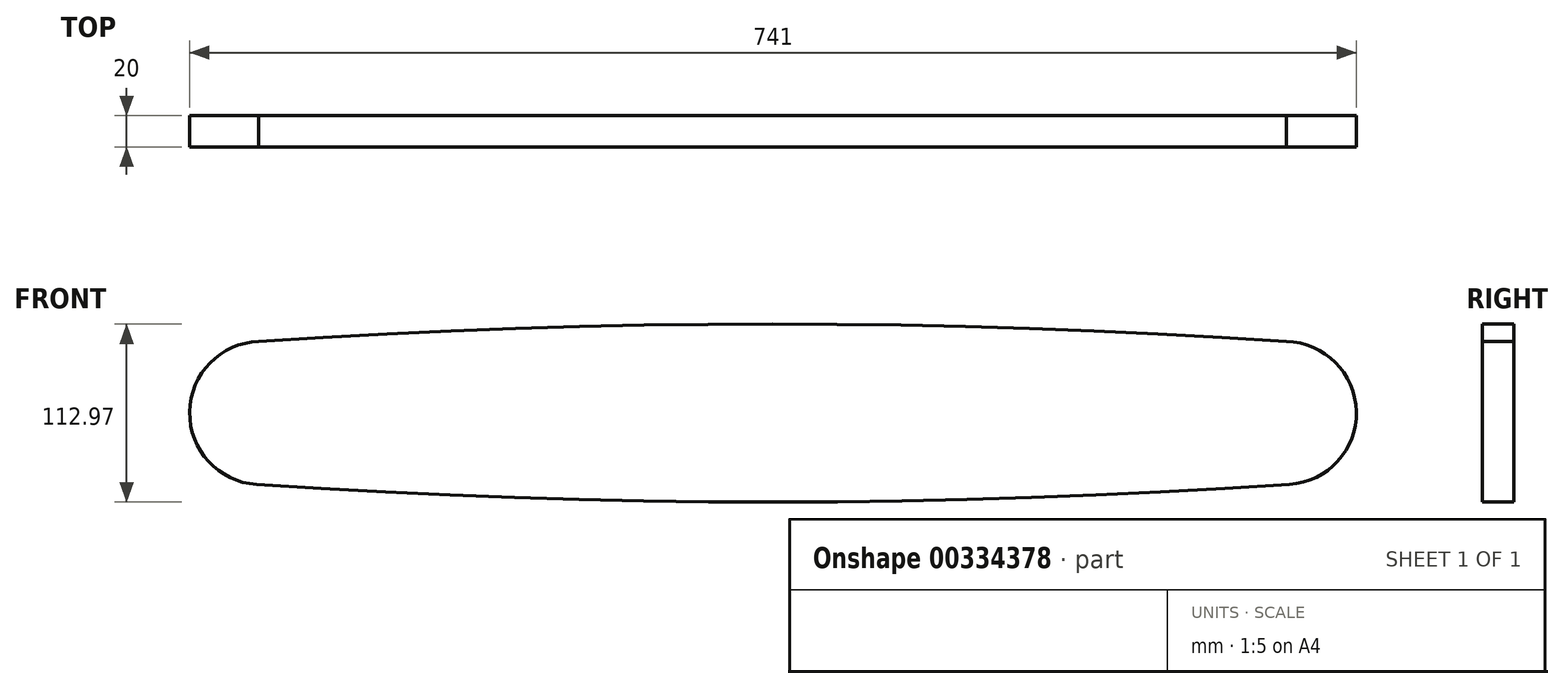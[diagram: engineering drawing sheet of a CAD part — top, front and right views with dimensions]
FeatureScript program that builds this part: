
annotation { "Feature Type Name" : "Feature", "Feature Type Description" : "" }
export const myFeature = defineFeature(function(context is Context, id is Id, definition is map)
    precondition{}
    {
        {
            var Q0;
            Q0=qCreatedBy(makeId("Front.planeOp"),FACE);
            var sketch = newSketch(context, id + "F0", { "sketchPlane" : qUnion([Q0])});
            skCircle(sketch, "E0", {"center": v(-325, 0) * mm, "radius": 45.5 * mm});
            skCircle(sketch, "E1", {"center": v(325, 0) * mm, "radius": 45.5 * mm});
            skLineSegment(sketch, "E2", {"start": v(-325, 0) * mm, "end": v(325, 0) * mm});
            skArc(sketch, "E3", {"start": v(-328.08, -45.4) * mm, "mid": v(0, -56.5) * mm, "end": v(328.08, -45.4) * mm});
            skPoint(sketch, "E3.centerSnap0", {"position": v(0, 0) * mm});
            skArc(sketch, "E4", {"start": v(325.96, 45.49) * mm, "mid": v(-0.31, 56.47) * mm, "end": v(-326.58, 45.47) * mm});
            skSolve(sketch);
        }
        {
            var Q0;
            {var subQ0=sQuery(id+"F0.wireOp",EDGE,"E4");Q0=makeQuery(id+"F0.imprint","IMPRINT",FACE,{"disambiguationData":[TD([[makeQuery(id+"F0.imprint","IMPRINT",EDGE,{"derivedFrom":subQ0}),1.0]])]});}
            var Q1;
            {var subQ0=sQuery(id+"F0.wireOp",EDGE,"E3");Q1=makeQuery(id+"F0.imprint","IMPRINT",FACE,{"disambiguationData":[TD([[makeQuery(id+"F0.imprint","IMPRINT",EDGE,{"derivedFrom":subQ0}),1.0]])]});}
            var Q2;
            {var subQ0=sQuery(id+"F0.wireOp",EDGE,"E0");var subQ1=makeQuery(id+"F0.imprint","INTERSECT",VERTEX,{"derivedFrom":[subQ0,sQuery(id+"F0.wireOp",EDGE,"E4")]});Q2=makeQuery(id+"F0.imprint","IMPRINT",FACE,{"disambiguationData":[TD([[makeQuery(id+"F0.imprint","IMPRINT",EDGE,{"disambiguationData":[TD([[subQ1,1.0]])],"derivedFrom":subQ0}),1.0]])]});}
            var Q3;
            {var subQ0=sQuery(id+"F0.wireOp",EDGE,"E1");var subQ1=makeQuery(id+"F0.imprint","INTERSECT",VERTEX,{"derivedFrom":[subQ0,sQuery(id+"F0.wireOp",EDGE,"E4")]});Q3=makeQuery(id+"F0.imprint","IMPRINT",FACE,{"disambiguationData":[TD([[makeQuery(id+"F0.imprint","IMPRINT",EDGE,{"disambiguationData":[TD([[subQ1,-1.0]])],"derivedFrom":subQ0}),1.0]])]});}
            extrude(context, id + "F1", {"entities" : qUnion([Q0, Q1, Q2, Q3]), "depth" : 20 * mm});
        }
    });
